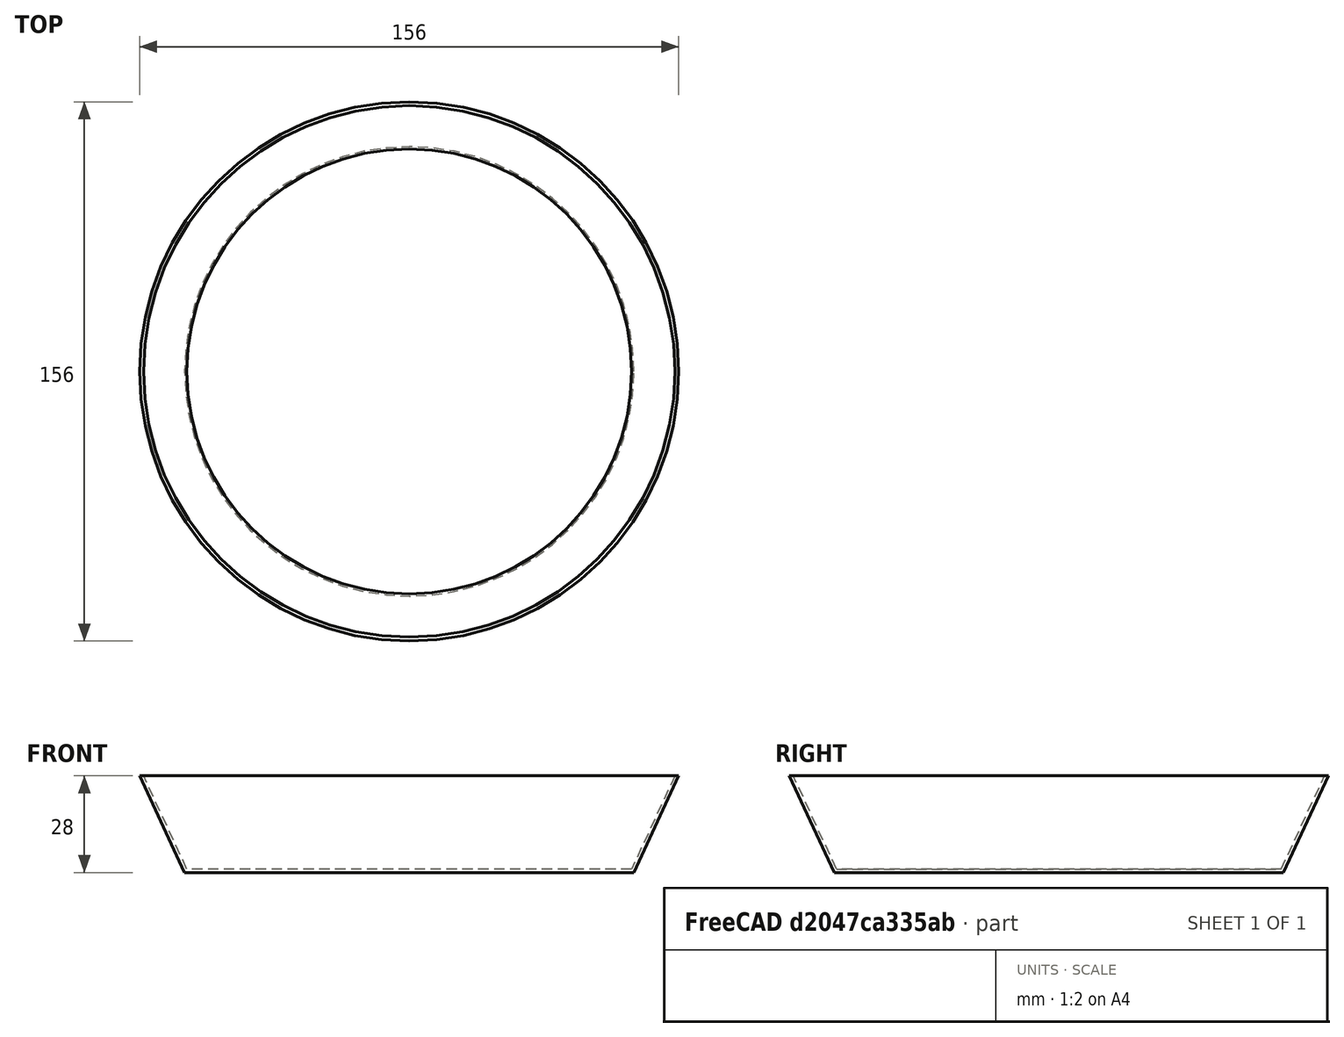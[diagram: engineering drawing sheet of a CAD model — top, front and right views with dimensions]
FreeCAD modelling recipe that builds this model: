
FCSTD DOCUMENT  (FreeCAD 0.20R29410 (Git))
Label: food_dish
License: All rights reserved
LicenseURL: http://en.wikipedia.org/wiki/All_rights_reserved
objects: Sketcher::SketchObject×1, PartDesign::Revolution×1, PartDesign::Body×1
note: 4 computed .brp shape members not serialized (recipe doc carries the construction recipe); baked Part::Feature solids carry a one-line shape summary decoded from their .brp

FEATURE [Sketcher::SketchObject] Sketch
  FullyConstrained = true
  MapMode = 5
  Placement = pos=(0,0,0) rot=(1,0,0;1.5708rad)
  Support = -> [XZ_Plane]
  sketch-geometry (8):
    g0: LineSegment StartX=0 StartY=0 StartZ=0 EndX=65 EndY=0 EndZ=0
    g1: LineSegment StartX=0 StartY=0 StartZ=0 EndX=0 EndY=1 EndZ=0
    g2: LineSegment StartX=0 StartY=1 StartZ=0 EndX=64.3618 EndY=1 EndZ=0
    g3: LineSegment StartX=65 StartY=0 StartZ=0 EndX=78 EndY=28 EndZ=0
    g4: LineSegment StartX=78 StartY=28 StartZ=0 EndX=76.8975 EndY=28 EndZ=0
    g5: LineSegment StartX=76.8975 StartY=28 StartZ=0 EndX=64.3618 EndY=1 EndZ=0
    g6: GeomPoint X=77.8045 Y=27.5789 Z=0
    g7: LineSegment StartX=76.8975 StartY=28 StartZ=0 EndX=77.8045 EndY=27.5789 EndZ=0
  constraints (21):
    c: Coincident(g0,g-1)
    c: PointOnObject(g0,g-1)
    c: DistanceX(g0) = 65
    c: Coincident(g1,g0)
    c: PointOnObject(g1,g-2)
    c: Coincident(g2,g1)
    c: Horizontal(g2)
    c: DistanceY(g1) = 1
    c: Coincident(g3,g0)
    c: Coincident(g4,g3)
    c: Coincident(g5,g4)
    c: Coincident(g5,g2)
    c: Parallel(g5,g3)
    c: Horizontal(g4)
    c: DistanceY(g3) = 28
    c: PointOnObject(g6,g3)
    c: Coincident(g7,g4)
    c: Coincident(g7,g6)
    c: Perpendicular(g5,g7)
    c: DistanceX(g3) = 78
    c: Distance(g7) = 1
FEATURE [PartDesign::Revolution] Revolution  label="food_dish"
  Angle = 360
  Axis = (-3e-16,3e-16,1)
  Base = (0,0,0)
  Placement = pos=(0,0,0) rot=(1,0,0;1.5708rad)
  Profile = -> Sketch
  ReferenceAxis = -> Z_Axis
  Reversed = true
FEATURE [PartDesign::Body] Body
  Group = -> [Sketch,Revolution]
  Origin = -> Origin
  Tip = -> Revolution
